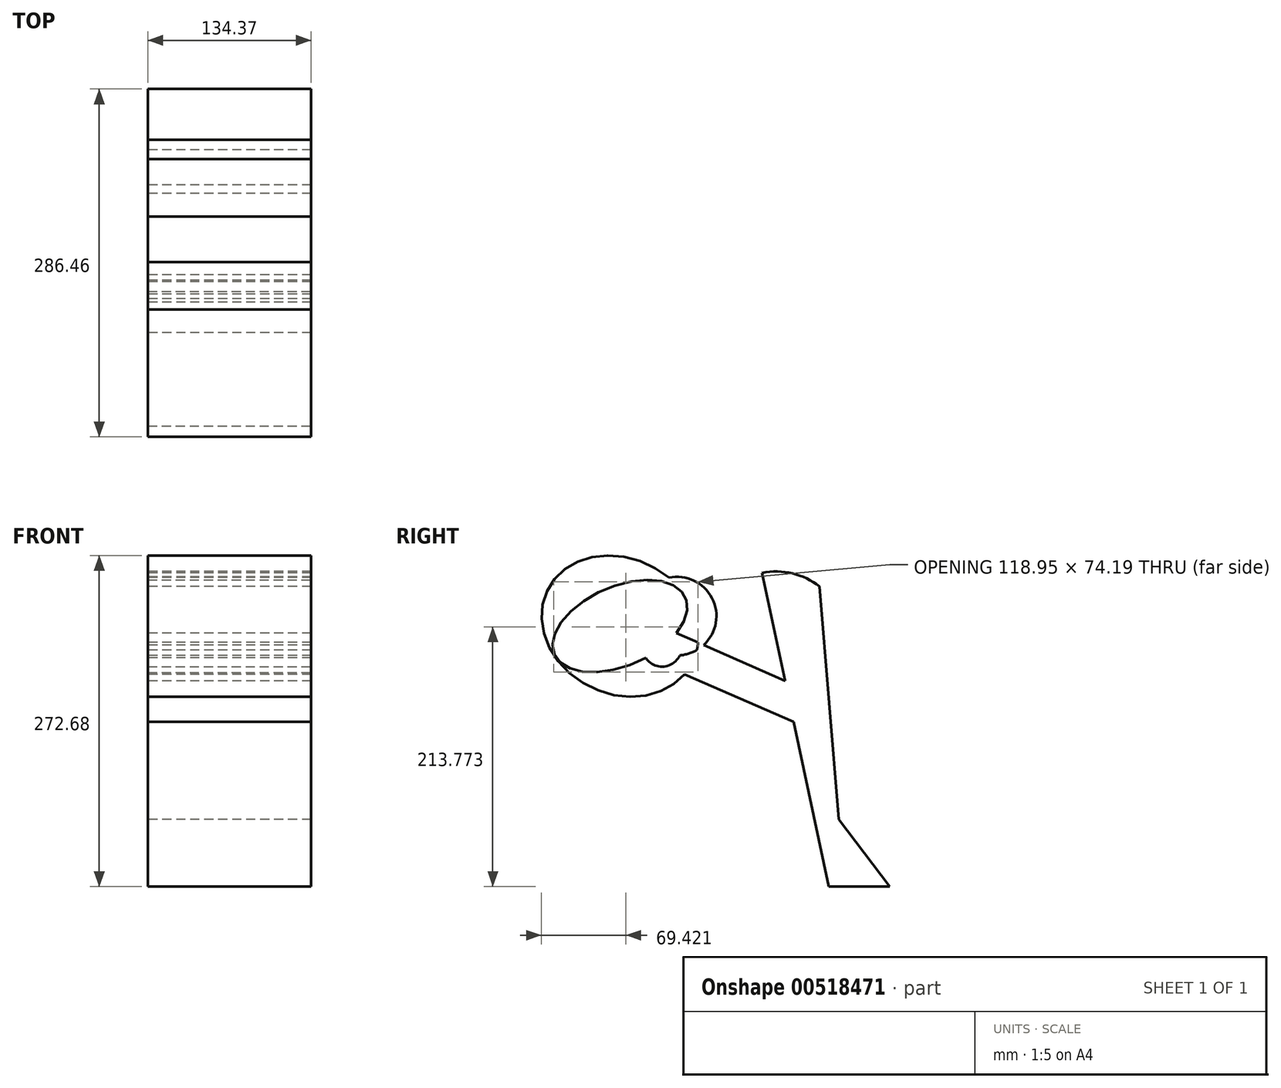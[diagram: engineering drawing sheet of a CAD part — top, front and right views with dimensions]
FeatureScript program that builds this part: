
annotation { "Feature Type Name" : "Feature", "Feature Type Description" : "" }
export const myFeature = defineFeature(function(context is Context, id is Id, definition is map)
    precondition{}
    {
        {
            var Q0;
            Q0=qCreatedBy(makeId("Right.planeOp"),FACE);
            var sketch = newSketch(context, id + "F0", { "sketchPlane" : qUnion([Q0])});
            skEllipse(sketch, "E0", {"center": v(0, 0) * mm, "majorRadius": 66.67 * mm, "minorRadius": 55.76 * mm, "majorAxis": v(0.9, -0.45)});
            skEllipse(sketch, "E1", {"center": v(0, 0) * mm, "majorRadius": 58.74 * mm, "minorRadius": 32.68 * mm, "majorAxis": v(0.92, 0.4)});
            skEllipse(sketch, "E2", {"center": v(34.8, -17.08) * mm, "majorRadius": 16 * mm, "minorRadius": 16.4 * mm, "majorAxis": v(0.9, -0.44)});
            skLineSegment(sketch, "E3", {"start": v(46.49, -5.64) * mm, "end": v(366.7, -146.9) * mm});
            skLineSegment(sketch, "E4", {"start": v(21.16, -26) * mm, "end": v(366.7, -175.92) * mm});
            skArc(sketch, "E5", {"start": v(49.2, -24.05) * mm, "mid": v(61.11, 37.28) * mm, "end": v(20.4, -10.1) * mm});
            skArc(sketch, "E6", {"start": v(164.32, 32.54) * mm, "mid": v(141.87, 43.3) * mm, "end": v(116.98, 43.89) * mm});
            skLineSegment(sketch, "E7", {"start": v(164.32, 32.54) * mm, "end": v(180.1, -159.2) * mm});
            skLineSegment(sketch, "E8", {"start": v(116.98, 43.89) * mm, "end": v(171.75, -214.51) * mm});
            skLineSegment(sketch, "E9", {"start": v(180.1, -159.2) * mm, "end": v(221.88, -214.51) * mm});
            skLineSegment(sketch, "E10", {"start": v(221.88, -214.51) * mm, "end": v(171.75, -214.51) * mm});
            skLineSegment(sketch, "E11", {"start": v(201, -186.86) * mm, "end": v(288.73, -206.54) * mm});
            skLineSegment(sketch, "E12", {"start": v(180.1, -159.2) * mm, "end": v(298.15, -210.4) * mm});
            skLineSegment(sketch, "E13", {"start": v(221.88, -214.51) * mm, "end": v(288.73, -206.54) * mm, "construction": true});
            skSolve(sketch);
        }
        {
            var Q0;
            Q0 = qSketchRegion(id + "F0", true);
            extrude(context, id + "F1", {"entities" : qUnion([Q0]), "depth" : 134.37 * mm, "offsetDistance" : 25.4 * mm});
        }
    });
